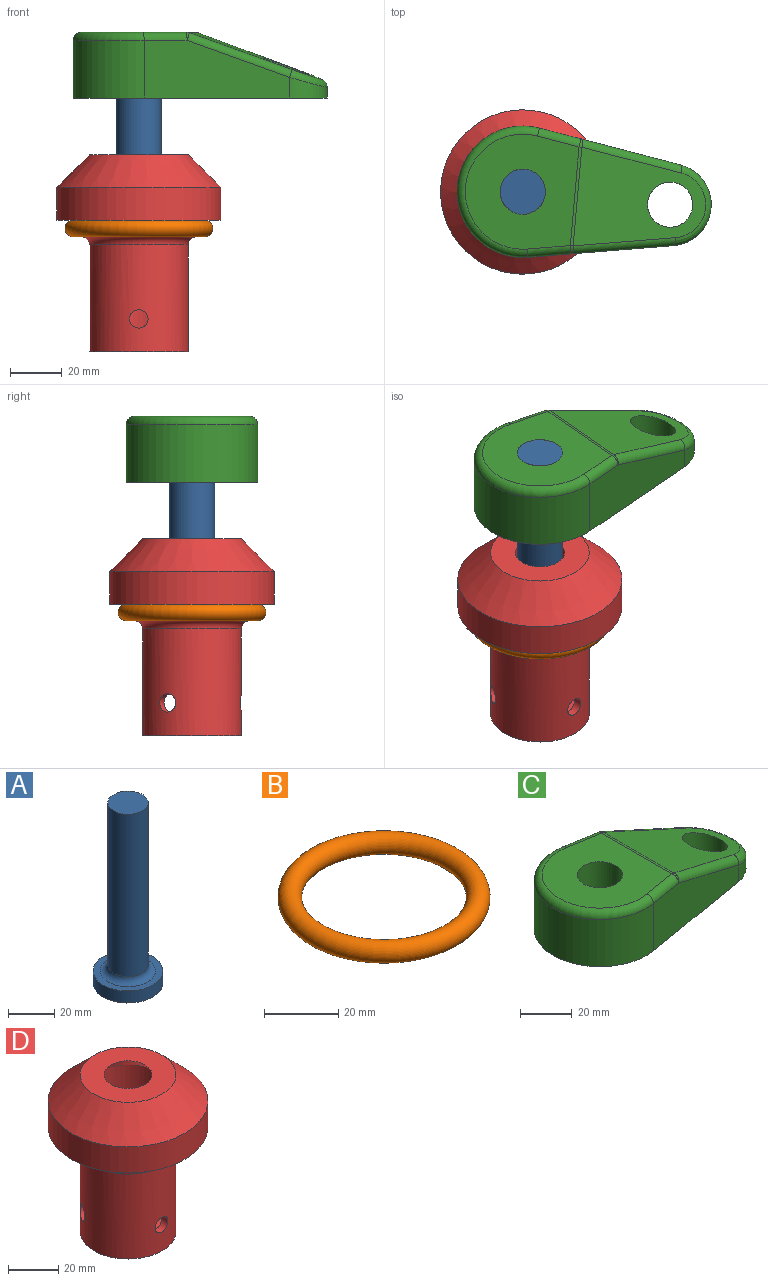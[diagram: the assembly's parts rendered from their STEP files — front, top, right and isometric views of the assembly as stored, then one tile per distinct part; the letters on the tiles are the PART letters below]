
ASSEMBLY  parts=4 mates=3
PART A: 6 faces, bbox 30.2x30.2x95.3 mm
  f0: plane 30.16x30.16mm, normal (0,0,-1), area 714.5mm2, adj f1
  f1: cylinder r=15.08mm len=30.16mm, axis (0,0,-1), area 601.7mm2, adj f0,f2
  f2: plane 30.16x30.16mm, normal (0,0,1), area 269.2mm2, adj f1,f5
  f3: cylinder r=8.73mm len=85.73mm, axis (0,0,-1), area 4702.9mm2, adj f4,f5
  f4: plane 17.46x17.46mm, normal (0,0,1), area 239.5mm2, adj f3
  f5: torus R=11.91mm, axis (0,0,-1), area 309.8mm2, adj f2,f3
PART B: 1 faces, bbox 61.9x61.9x6.4 mm
  f0: torus R=25.4mm, axis (0,0,1), area 3183.7mm2
PART C: 18 faces, bbox 101.9x56.3x26.7 mm
  f0: plane 98.43x50.8mm, normal (0,0,-1), area 3322mm2, adj f1,f3,f4,f5,f6,f7
  f1: plane 55.56x22.23mm, normal (0.17,-0.99,0), area 969.6mm2, adj f0,f5,f6,f9,f14
  f2: plane 44.45x42.35mm, normal (0,0,1), area 1374.4mm2, adj f4,f9,f10,f12,f13
  f3: cylinder r=8.73mm len=17.46mm, axis (0,0,1), area 665.3mm2, adj f0,f8
  f4: cylinder r=8.73mm len=25.4mm, axis (0,0,1), area 1393.4mm2, adj f0,f2
  f5: cylinder r=25.4mm len=50.8mm, axis (0,0,1), area 1962.5mm2, adj f0,f1,f7,f10
  f6: cylinder r=15.88mm len=31.31mm, axis (0,0,1), area 245.1mm2, adj f0,f1,f7,f16
  f7: plane 55.56x22.23mm, normal (0.17,0.99,0), area 969.6mm2, adj f0,f5,f6,f13,f17
  f8: plane 51.06x39.61mm, normal (0.34,0,0.94), area 1276.6mm2, adj f3,f12,f14,f16,f17
  f9: cylinder r=3.17mm len=16.95mm, axis (0.99,0.17,0), area 83.1mm2, adj f1,f2,f10,f11
  f10: torus R=22.23mm, axis (0,0,1), area 420.4mm2, adj f2,f5,f9,f13
  f11: sphere r=3.17mm, area 3.1mm2, adj f9,f12,f14
  f12: cylinder r=3.17mm len=38.28mm, axis (0,1,0), area 42.4mm2, adj f2,f8,f11,f15
  f13: cylinder r=3.17mm len=16.95mm, axis (-0.99,0.17,0), area 83.1mm2, adj f2,f7,f10,f15
  f14: cylinder r=3.17mm len=39.79mm, axis (-0.93,-0.16,0.34), area 202.7mm2, adj f1,f8,f11,f16
  f15: sphere r=3.17mm, area 3.4mm2, adj f12,f13,f17
  f16: bspline ~31.31x13.22mm, area 176.2mm2, adj f6,f8,f14,f17
  f17: cylinder r=3.17mm len=39.79mm, axis (0.93,-0.16,-0.34), area 202.7mm2, adj f7,f8,f15,f16
PART D: 16 faces, bbox 63.5x63.5x76.2 mm
  f0: cylinder r=19.05mm len=41.28mm, axis (0,0,1), area 4819.4mm2, adj f2,f10,f11,f12,f13
  f1: cylinder r=15.88mm len=63.5mm, axis (0,0,1), area 6212.7mm2, adj f8,f9,f10,f11,f12
  f2: plane 38.1x38.1mm, normal (0,0,-1), area 1013.4mm2, adj f0,f15
  f3: cylinder r=22.23mm len=44.45mm, axis (0,0,1), area 443.4mm2, adj f13,f14
  f4: plane 63.5x63.5mm, normal (0,0,-1), area 1140.1mm2, adj f5,f14
  f5: cylinder r=31.75mm len=63.5mm, axis (0,0,1), area 2533.5mm2, adj f4,f6
  f6: cone r=19.05mm half-angle=45deg, axis (0,0,-1), area 2866.4mm2, adj f5,f7
  f7: plane 38.1x38.1mm, normal (0,0,1), area 855.1mm2, adj f6,f8
  f8: cone r=9.53mm half-angle=45deg, axis (0,0,-1), area 716.6mm2, adj f1,f7
  f9: plane 31.75x31.75mm, normal (0,0,1), area 665.1mm2, adj f1,f15
  f10: cylinder r=3.57mm len=7.14mm, axis (0,1,0), area 72mm2, adj f0,f1
  f11: cylinder r=3.57mm len=7.97mm, axis (-0.87,-0.5,0), area 72mm2, adj f0,f1
  f12: cylinder r=3.57mm len=7.97mm, axis (0.87,-0.5,0), area 72mm2, adj f0,f1
  f13: torus R=22.23mm, axis (0,0,-1), area 633.1mm2, adj f0,f3
  f14: torus R=25.4mm, axis (0,0,-1), area 732.6mm2, adj f3,f4
  f15: cylinder r=6.35mm len=12.7mm, axis (0,0,-1), area 253.4mm2, adj f2,f9
PLACE A rot(axis=(0,0,1),85deg) t=(0,0,21.84)mm
PLACE B t=(0,0,47.63)mm
PLACE C rot(axis=(0,0,-1),5deg) t=(0,0,21.84)mm
PLACE D at identity fixed
MATE fastened A.f1 <-> C.f4  axis (0,0,1) through (0,0,123.44)mm
MATE cylindrical A.f1 <-> D.f0  axis (0,0,-1) through (0,0,28.19)mm
MATE fastened B.f0 <-> D.f0  axis (0,0,1) through (0,0,47.63)mm
